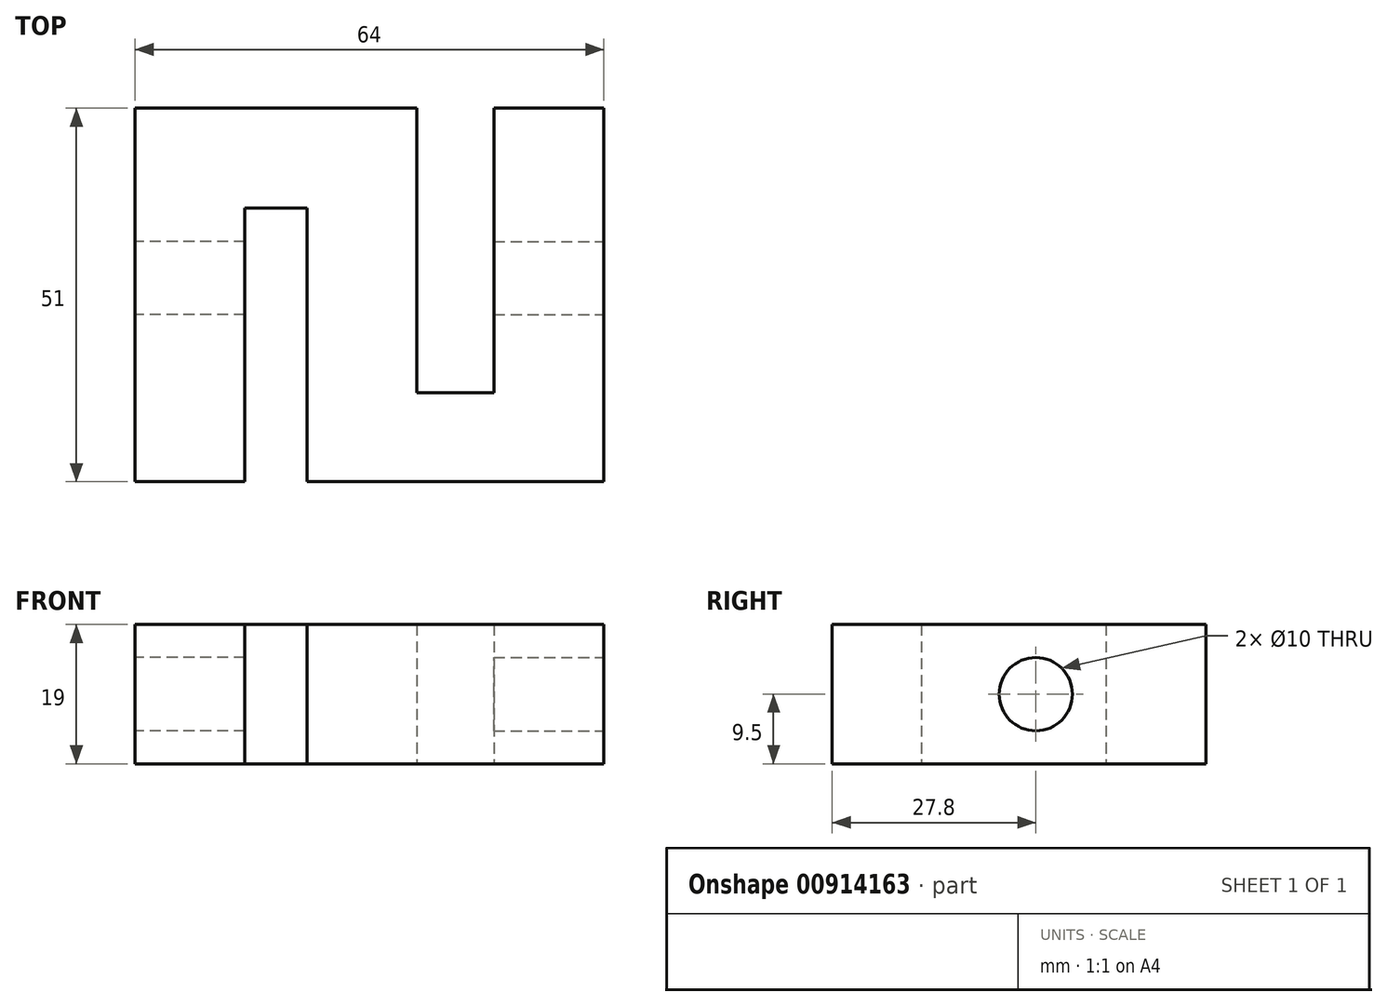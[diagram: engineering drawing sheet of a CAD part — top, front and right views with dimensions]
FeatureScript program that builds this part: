
annotation { "Feature Type Name" : "Feature", "Feature Type Description" : "" }
export const myFeature = defineFeature(function(context is Context, id is Id, definition is map)
    precondition{}
    {
        {
            var Q0;
            Q0=qCreatedBy(makeId("Top.planeOp"),FACE);
            var sketch = newSketch(context, id + "F0", { "sketchPlane" : qUnion([Q0])});
            skLineSegment(sketch, "E0.bottom", {"start": v(-35.38, 23.2) * mm, "end": v(3.12, 23.2) * mm});
            skLineSegment(sketch, "E0.top", {"start": v(-35.38, -27.8) * mm, "end": v(-20.38, -27.8) * mm});
            skLineSegment(sketch, "E0.left", {"start": v(-35.38, 23.2) * mm, "end": v(-35.38, -27.8) * mm});
            skLineSegment(sketch, "E0.right", {"start": v(28.62, 23.2) * mm, "end": v(28.62, -27.8) * mm});
            skLineSegment(sketch, "E1", {"start": v(-20.38, -27.8) * mm, "end": v(-20.38, 9.55) * mm});
            skLineSegment(sketch, "E2", {"start": v(-20.38, 9.55) * mm, "end": v(-11.88, 9.55) * mm});
            skLineSegment(sketch, "E3", {"start": v(-11.88, 9.55) * mm, "end": v(-11.88, -27.8) * mm});
            skLineSegment(sketch, "E4", {"start": v(3.12, 23.2) * mm, "end": v(3.12, -15.65) * mm});
            skLineSegment(sketch, "E5", {"start": v(3.12, -15.65) * mm, "end": v(13.62, -15.65) * mm});
            skLineSegment(sketch, "E6", {"start": v(13.62, 23.2) * mm, "end": v(13.62, -15.65) * mm});
            skLineSegment(sketch, "E7.trimOffspring", {"start": v(13.62, 23.2) * mm, "end": v(28.62, 23.2) * mm});
            skLineSegment(sketch, "E8.trimOffspring", {"start": v(-11.88, -27.8) * mm, "end": v(28.62, -27.8) * mm});
            skSolve(sketch);
        }
        {
            var Q0;
            Q0 = qSketchRegion(id + "F0", true);
            extrude(context, id + "F1", {"entities" : qUnion([Q0]), "depth" : 19 * mm, "offsetDistance" : 25 * mm});
        }
        {
            var Q0;
            Q0=makeQuery(id+"F1.opExtrude","SWEPT_FACE",FACE,{"disambiguationData":[OSD([sQuery(id+"F0.wireOp",EDGE,"E0.right")])]});
            cPlane(context, id + "F2", {"entities" : qUnion([Q0]), "cplaneType" : CPlaneType.OFFSET, "offset" : 0 * mm, "oppositeDirection" : true, "width" : 150 * mm, "height" : 150 * mm});
        }
        {
            var Q0;
            Q0=qCreatedBy(id+"F2.planeOp",FACE);
            var sketch = newSketch(context, id + "F3", { "sketchPlane" : qUnion([Q0])});
            skCircle(sketch, "E9", {"center": v(0, 9.5) * mm, "radius": 5 * mm});
            skSolve(sketch);
        }
        {
            var Q0;
            Q0=makeQuery(id+"F3.imprint","IMPRINT",FACE,{"disambiguationData":[TD([[makeQuery(id+"F3.imprint","IMPRINT",EDGE,{"derivedFrom":sQuery(id+"F3.wireOp",EDGE,"E9")}),1.0]])]});
            extrude(context, id + "F4", {"entities" : qUnion([Q0]), "operationType" : NewBodyOperationType.REMOVE, "oppositeDirection" : true, "depth" : 16 * mm, "offsetDistance" : 25 * mm});
        }
        {
            var Q0;
            Q0=makeQuery(id+"F1.opExtrude","SWEPT_FACE",FACE,{"disambiguationData":[OSD([sQuery(id+"F0.wireOp",EDGE,"E0.left")])]});
            cPlane(context, id + "F5", {"entities" : qUnion([Q0]), "cplaneType" : CPlaneType.OFFSET, "offset" : 0 * mm, "width" : 150 * mm, "height" : 150 * mm});
        }
        {
            var Q0;
            Q0=qCreatedBy(id+"F5.planeOp",FACE);
            var sketch = newSketch(context, id + "F6", { "sketchPlane" : qUnion([Q0])});
            skCircle(sketch, "E10", {"center": v(0, 9.5) * mm, "radius": 5 * mm});
            skSolve(sketch);
        }
        {
            var Q0;
            Q0=makeQuery(id+"F6.imprint","IMPRINT",FACE,{"disambiguationData":[TD([[makeQuery(id+"F6.imprint","IMPRINT",EDGE,{"derivedFrom":sQuery(id+"F6.wireOp",EDGE,"E10")}),1.0]])]});
            extrude(context, id + "F7", {"entities" : qUnion([Q0]), "operationType" : NewBodyOperationType.REMOVE, "oppositeDirection" : true, "depth" : 16 * mm, "offsetDistance" : 25 * mm});
        }
    });
